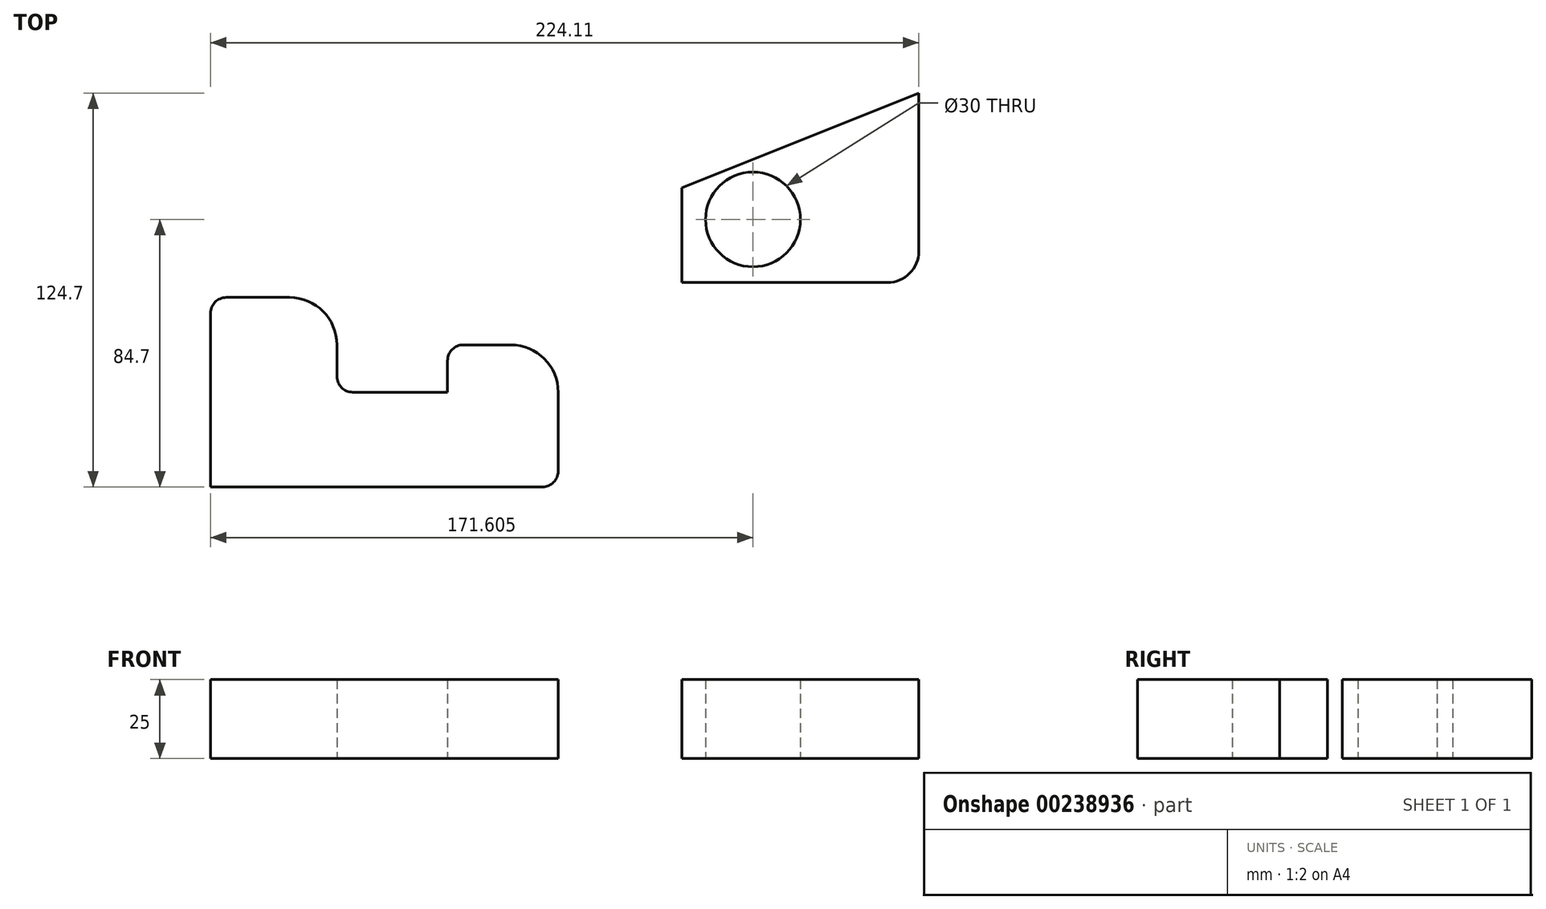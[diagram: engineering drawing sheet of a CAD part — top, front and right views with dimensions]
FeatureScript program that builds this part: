
annotation { "Feature Type Name" : "Feature", "Feature Type Description" : "" }
export const myFeature = defineFeature(function(context is Context, id is Id, definition is map)
    precondition{}
    {
        {
            var Q0;
            Q0=qCreatedBy(makeId("Top.planeOp"),FACE);
            var sketch = newSketch(context, id + "F0", { "sketchPlane" : qUnion([Q0])});
            skLineSegment(sketch, "E0", {"start": v(-62.34, -64.54) * mm, "end": v(42.66, -64.54) * mm});
            skLineSegment(sketch, "E1", {"start": v(47.66, -59.54) * mm, "end": v(47.66, -34.54) * mm});
            skLineSegment(sketch, "E2", {"start": v(32.66, -19.54) * mm, "end": v(17.66, -19.54) * mm});
            skLineSegment(sketch, "E3", {"start": v(12.66, -24.54) * mm, "end": v(12.66, -34.54) * mm});
            skLineSegment(sketch, "E4", {"start": v(12.66, -34.54) * mm, "end": v(-17.34, -34.54) * mm});
            skLineSegment(sketch, "E5", {"start": v(-22.34, -29.54) * mm, "end": v(-22.34, -19.54) * mm});
            skLineSegment(sketch, "E6", {"start": v(-37.34, -4.54) * mm, "end": v(-57.34, -4.54) * mm});
            skLineSegment(sketch, "E7", {"start": v(-62.34, -9.54) * mm, "end": v(-62.34, -64.54) * mm});
            skPoint(sketch, "E8.visualSharp", {"position": v(-62.34, -4.54) * mm});
            skArc(sketch, "E8.filletArc", {"start": v(-57.34, -4.54) * mm, "mid": v(-60.87, -6) * mm, "end": v(-62.34, -9.54) * mm});
            skPoint(sketch, "E9.visualSharp", {"position": v(-22.34, -4.54) * mm});
            skArc(sketch, "E9.filletArc", {"start": v(-22.34, -19.54) * mm, "mid": v(-26.73, -8.93) * mm, "end": v(-37.34, -4.54) * mm});
            skPoint(sketch, "E10.visualSharp", {"position": v(-22.34, -34.54) * mm});
            skArc(sketch, "E10.filletArc", {"start": v(-22.34, -29.54) * mm, "mid": v(-20.87, -33.08) * mm, "end": v(-17.34, -34.54) * mm});
            skPoint(sketch, "E11.visualSharp", {"position": v(12.66, -19.54) * mm});
            skArc(sketch, "E11.filletArc", {"start": v(17.66, -19.54) * mm, "mid": v(14.13, -21) * mm, "end": v(12.66, -24.54) * mm});
            skPoint(sketch, "E12.visualSharp", {"position": v(47.66, -19.54) * mm});
            skArc(sketch, "E12.filletArc", {"start": v(47.66, -34.54) * mm, "mid": v(43.27, -23.93) * mm, "end": v(32.66, -19.54) * mm});
            skPoint(sketch, "E13.visualSharp", {"position": v(47.66, -64.54) * mm});
            skArc(sketch, "E13.filletArc", {"start": v(42.66, -64.54) * mm, "mid": v(46.2, -63.08) * mm, "end": v(47.66, -59.54) * mm});
            skLineSegment(sketch, "E14", {"start": v(86.77, 30.16) * mm, "end": v(86.77, 0.16) * mm});
            skLineSegment(sketch, "E15", {"start": v(86.77, 0.16) * mm, "end": v(151.77, 0.16) * mm});
            skLineSegment(sketch, "E16", {"start": v(161.77, 10.16) * mm, "end": v(161.77, 60.16) * mm});
            skLineSegment(sketch, "E17", {"start": v(161.77, 60.16) * mm, "end": v(86.77, 30.16) * mm});
            skPoint(sketch, "E18.visualSharp", {"position": v(161.77, 0.16) * mm});
            skArc(sketch, "E18.filletArc", {"start": v(151.77, 0.16) * mm, "mid": v(158.84, 3.09) * mm, "end": v(161.77, 10.16) * mm});
            skCircle(sketch, "E19", {"center": v(109.27, 20.16) * mm, "radius": 15 * mm});
            skSolve(sketch);
        }
        {
            var Q0;
            Q0=makeQuery(id+"F0.imprint","IMPRINT",FACE,{"disambiguationData":[TD([[makeQuery(id+"F0.imprint","IMPRINT",EDGE,{"derivedFrom":sQuery(id+"F0.wireOp",EDGE,"E14")}),1.0]])]});
            var Q1;
            Q1=makeQuery(id+"F0.imprint","IMPRINT",FACE,{"disambiguationData":[TD([[makeQuery(id+"F0.imprint","IMPRINT",EDGE,{"derivedFrom":sQuery(id+"F0.wireOp",EDGE,"E0")}),1.0]])]});
            extrude(context, id + "F1", {"entities" : qUnion([Q0, Q1]), "depth" : 25 * mm});
        }
    });
